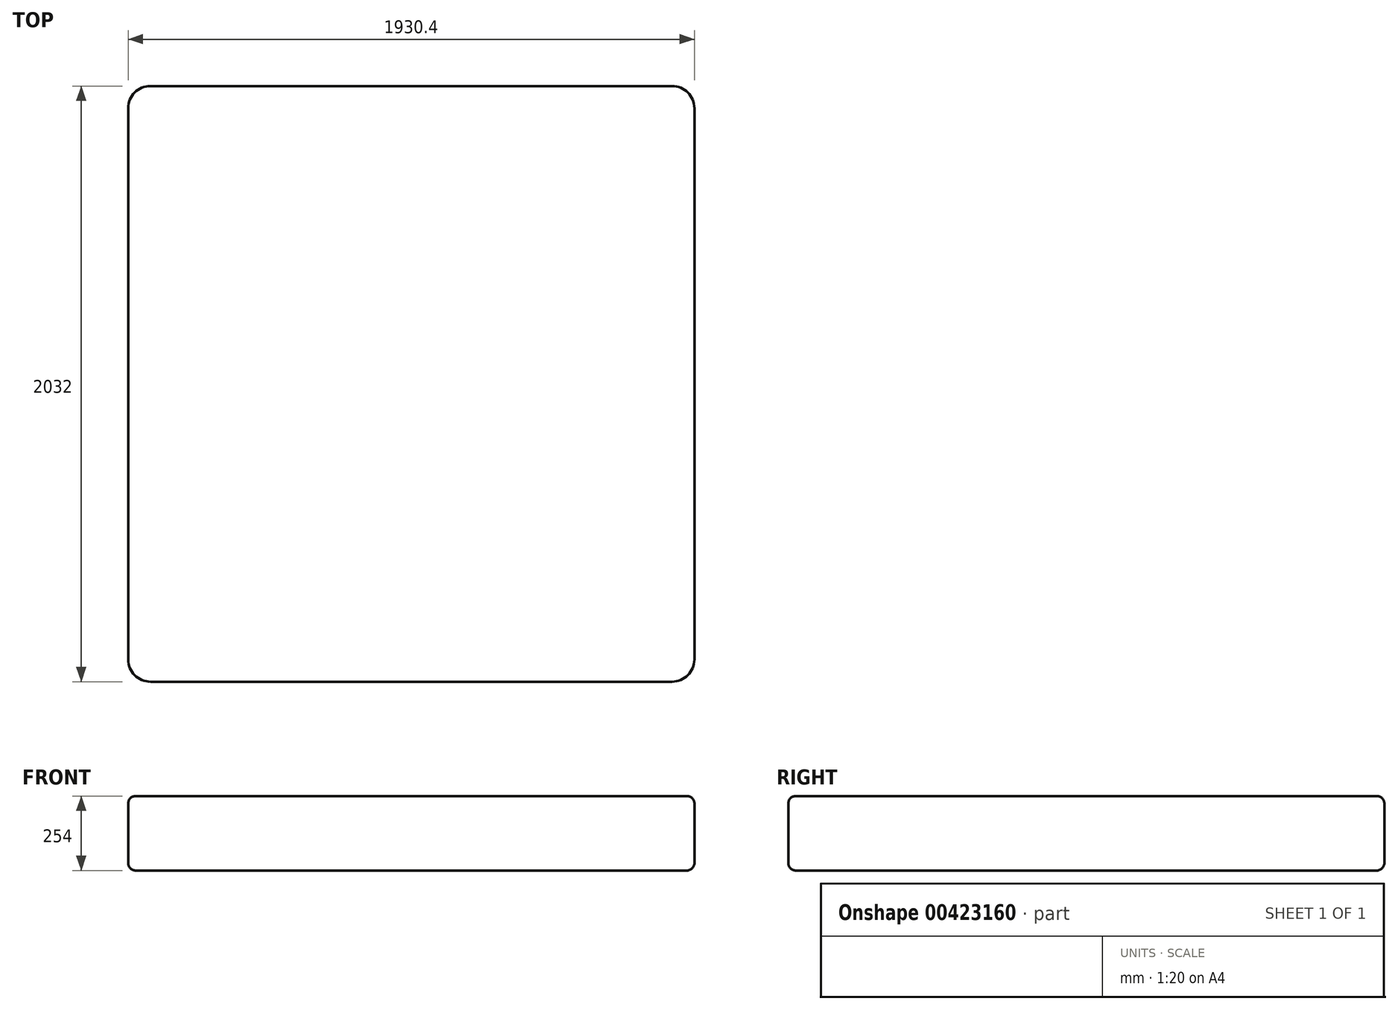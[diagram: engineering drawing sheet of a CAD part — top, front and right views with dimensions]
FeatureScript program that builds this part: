
annotation { "Feature Type Name" : "Feature", "Feature Type Description" : "" }
export const myFeature = defineFeature(function(context is Context, id is Id, definition is map)
    precondition{}
    {
        {
            var Q0;
            Q0=qCreatedBy(makeId("Top.planeOp"),FACE);
            var sketch = newSketch(context, id + "F0", { "sketchPlane" : qUnion([Q0])});
            skLineSegment(sketch, "E0.bottom", {"start": v(-965.2, -1016) * mm, "end": v(965.2, -1016) * mm});
            skLineSegment(sketch, "E0.top", {"start": v(-965.2, 1016) * mm, "end": v(965.2, 1016) * mm});
            skLineSegment(sketch, "E0.left", {"start": v(-965.2, -1016) * mm, "end": v(-965.2, 1016) * mm});
            skLineSegment(sketch, "E0.right", {"start": v(965.2, -1016) * mm, "end": v(965.2, 1016) * mm});
            skPoint(sketch, "E0.middle", {"position": v(0, 0) * mm});
            skSolve(sketch);
        }
        {
            var Q0;
            Q0=makeQuery(id+"F0.imprint","IMPRINT",FACE,{"disambiguationData":[TD([[makeQuery(id+"F0.imprint","IMPRINT",EDGE,{"derivedFrom":sQuery(id+"F0.wireOp",EDGE,"E0.bottom")}),1.0]])]});
            extrude(context, id + "F1", {"entities" : qUnion([Q0]), "depth" : 254 * mm});
        }
        {
            var Q0;
            Q0=makeQuery(id+"F1.opExtrude","CAP_EDGE",EDGE,{"disambiguationData":[OSD([sQuery(id+"F0.wireOp",EDGE,"E0.bottom")])],"isStart":false});
            var Q1;
            Q1=makeQuery(id+"F1.opExtrude","CAP_EDGE",EDGE,{"disambiguationData":[OSD([sQuery(id+"F0.wireOp",EDGE,"E0.right")])],"isStart":false});
            var Q2;
            Q2=makeQuery(id+"F1.opExtrude","CAP_EDGE",EDGE,{"disambiguationData":[OSD([sQuery(id+"F0.wireOp",EDGE,"E0.top")])],"isStart":false});
            var Q3;
            Q3=makeQuery(id+"F1.opExtrude","CAP_EDGE",EDGE,{"disambiguationData":[OSD([sQuery(id+"F0.wireOp",EDGE,"E0.left")])],"isStart":false});
            var Q4;
            Q4=makeQuery(id+"F1.opExtrude","CAP_EDGE",EDGE,{"disambiguationData":[OSD([sQuery(id+"F0.wireOp",EDGE,"E0.bottom")])],"isStart":true});
            var Q5;
            Q5=makeQuery(id+"F1.opExtrude","CAP_EDGE",EDGE,{"disambiguationData":[OSD([sQuery(id+"F0.wireOp",EDGE,"E0.right")])],"isStart":true});
            var Q6;
            Q6=makeQuery(id+"F1.opExtrude","CAP_EDGE",EDGE,{"disambiguationData":[OSD([sQuery(id+"F0.wireOp",EDGE,"E0.top")])],"isStart":true});
            var Q7;
            Q7=makeQuery(id+"F1.opExtrude","CAP_EDGE",EDGE,{"disambiguationData":[OSD([sQuery(id+"F0.wireOp",EDGE,"E0.left")])],"isStart":true});
            fillet(context, id + "F2", {"entities" : qUnion([Q0, Q1, Q2, Q3, Q4, Q5, Q6, Q7]), "radius" : 25.4 * mm, "tangentPropagation" : true, "allowEdgeOverflow" : false});
        }
        {
            var Q0;
            Q0=makeQuery(id+"F1.opExtrude","SWEPT_EDGE",EDGE,{"disambiguationData":[OSD([sQuery(id+"F0.wireOp",EDGE,"E0.bottom"),sQuery(id+"F0.wireOp",EDGE,"E0.right")])]});
            var Q1;
            Q1=makeQuery(id+"F1.opExtrude","SWEPT_EDGE",EDGE,{"disambiguationData":[OSD([sQuery(id+"F0.wireOp",EDGE,"E0.top"),sQuery(id+"F0.wireOp",EDGE,"E0.right")])]});
            var Q2;
            Q2=makeQuery(id+"F1.opExtrude","SWEPT_EDGE",EDGE,{"disambiguationData":[OSD([sQuery(id+"F0.wireOp",EDGE,"E0.bottom"),sQuery(id+"F0.wireOp",EDGE,"E0.left")])]});
            var Q3;
            Q3=makeQuery(id+"F1.opExtrude","SWEPT_EDGE",EDGE,{"disambiguationData":[OSD([sQuery(id+"F0.wireOp",EDGE,"E0.top"),sQuery(id+"F0.wireOp",EDGE,"E0.left")])]});
            fillet(context, id + "F3", {"entities" : qUnion([Q0, Q1, Q2, Q3]), "radius" : 76.2 * mm, "tangentPropagation" : true, "allowEdgeOverflow" : false});
        }
    });
